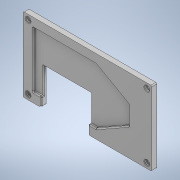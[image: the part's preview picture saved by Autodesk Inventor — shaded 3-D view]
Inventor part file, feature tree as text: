
AUTODESK INVENTOR PART (.ipt)
format: ipt  version: 2020 (Build 240168000, 168)  size: 251,904 bytes
history: native  units: in
note: dims shown in document units (in); Inventor stores cm internally (conversion verified against a paired STEP export)
features: fillet x8, sketch x4, extrude x3, chamfer x2
ambient origin geometry x8: Origin, YZ Plane, XZ Plane, XY Plane, X Axis, Y Axis, Z Axis, Center Point
bodies: Solid1 (feature_tree), Body1 (feature_tree)
feature tree (17):
  sketch  "Sketch1"  dims[d0=3.7402in d1=0.1969in d2=0.0in d3=0.0in d4=3.7402in d5=0.0in]
  extrude  "Extrusion1"  Depth=0.1969in TaperAngle=0.0deg
  extrude  "Extrusion2"  Depth=2.7559in TaperAngle=0.0deg
  extrude  "Extrusion3"  Depth=0.0787in TaperAngle=45.0deg
  chamfer  "Chamfer1"  Distance=0.0787in
  chamfer  "Chamfer2"  Distance=0.0787in
  fillet  "Fillet1"  Radius=0.0787in
  fillet  "Fillet2"  Radius=0.0787in
  fillet  "Fillet3"  Radius=0.0787in
  fillet  "Fillet4"  Radius=0.0787in
  fillet  "Fillet5"  Radius=0.0787in
  fillet  "Fillet6"  [1 undecoded]
  fillet  "Fillet7"  [1 undecoded]
  fillet  "Fillet8"  [1 undecoded]
  sketch  "Sketch2"  dims[d8=1.4335in d9=2.7559in d10=0.0in]
  sketch  "Sketch3"  dims[d11=0.0787in d12=0.0787in d13=45.0deg d14=0.0787in d15=0.0787in d16=45.0deg]
  sketch  "Sketch6"  dims[d17=0.0787in d18=0.0787in d19=0.0787in d20=0.0787in d21=0.0787in d22=0.0787in d23=0.0787in d24=0.0787in]
note: 3 required parameter values undecoded (feature->parameter linkage not recoverable at this tier; creation-order binding heuristic only, values carry confidence <= 0.55)
